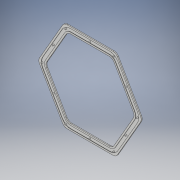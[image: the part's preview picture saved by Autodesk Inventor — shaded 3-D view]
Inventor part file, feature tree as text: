
AUTODESK INVENTOR PART (.ipt)
format: ipt  version: 2019 (Build 230136000, 136)  size: 454,144 bytes
history: native  units: mm
features: extrude x4, sketch x3, projected_geometry x3, fillet x2
ambient origin geometry x8: Origin, YZ Plane, XZ Plane, XY Plane, X Axis, Y Axis, Z Axis, Center Point
bodies: Solid1 (feature_tree)
feature tree (12):
  extrude  "Extrusion1"  Depth=2.0mm TaperAngle=0.0deg
  extrude  "Extrusion6"  Depth=10.0mm
  fillet  "Fillet2"  Radius=10.0mm
  fillet  "Fillet3"  Radius=12.0mm
  extrude  "Extrusion8"  Depth=2.0mm
  extrude  "Extrusion9"  Depth=3.0mm
  sketch  "Sketch1"  dims[d0=175.0mm d1=2.0mm d2=0.0mm]
  sketch  "Sketch7"  dims[d20=7.0mm d21=0.0mm d24=10.0mm d25=10.0mm d26=12.0mm]
  projected_geometry  "Projected Loop7"
  projected_geometry  "Projected Loop9"
  sketch  "Sketch10"  dims[d44=3.0mm d50=2.0mm d51=-1.745329mm d52=3.0mm d53=6.0mm d54=0.7mm d55=0.0mm d56=60.0mm d58=360.0deg]
  projected_geometry  "Projected Loop10"
